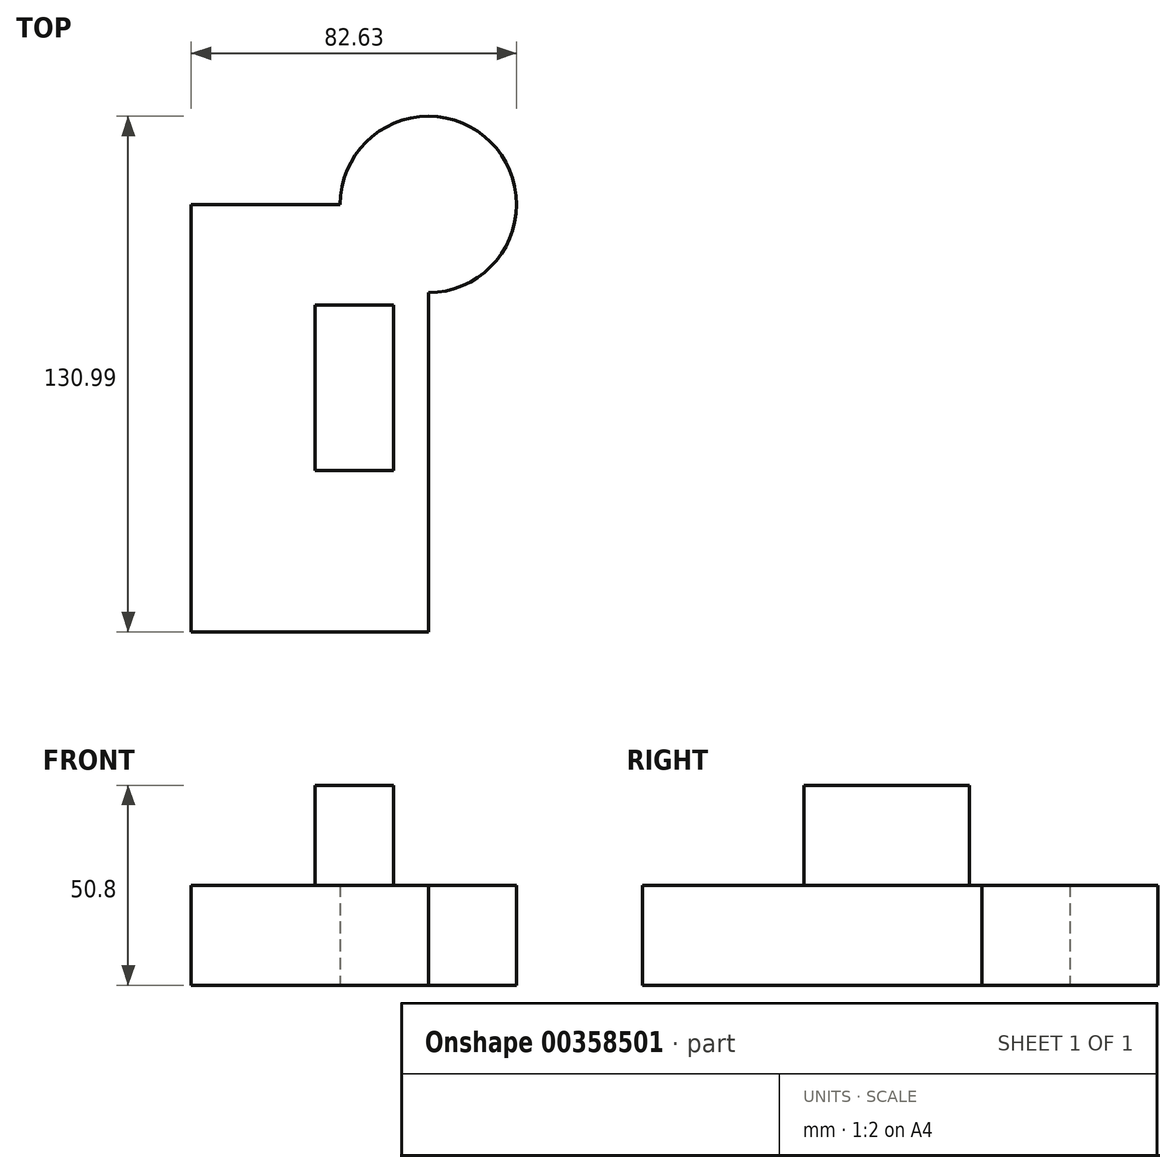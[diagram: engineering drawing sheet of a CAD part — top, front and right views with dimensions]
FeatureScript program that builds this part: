
annotation { "Feature Type Name" : "Feature", "Feature Type Description" : "" }
export const myFeature = defineFeature(function(context is Context, id is Id, definition is map)
    precondition{}
    {
        {
            var Q0;
            Q0=qCreatedBy(makeId("Top.planeOp"),FACE);
            var sketch = newSketch(context, id + "F0", { "sketchPlane" : qUnion([Q0])});
            skLineSegment(sketch, "E0.bottom", {"start": v(2.73, -58.58) * mm, "end": v(62.95, -58.58) * mm});
            skLineSegment(sketch, "E0.top", {"start": v(2.73, 50) * mm, "end": v(62.95, 50) * mm});
            skLineSegment(sketch, "E0.left", {"start": v(2.73, -58.58) * mm, "end": v(2.73, 50) * mm});
            skLineSegment(sketch, "E0.right", {"start": v(62.95, -58.58) * mm, "end": v(62.95, 50) * mm});
            skCircle(sketch, "E1", {"center": v(62.95, 50) * mm, "radius": 22.4 * mm});
            skSolve(sketch);
        }
        {
            var Q0;
            Q0 = qSketchRegion(id + "F0", true);
            extrude(context, id + "F1", {"entities" : qUnion([Q0]), "depth" : 25.4 * mm});
        }
        {
            var Q0;
            Q0=makeQuery(id+"F1.opExtrude","CAP_FACE",FACE,{"disambiguationData":[OSD([sQuery(id+"F0.wireOp",EDGE,"E0.bottom"),sQuery(id+"F0.wireOp",EDGE,"E0.top"),sQuery(id+"F0.wireOp",EDGE,"E0.left"),sQuery(id+"F0.wireOp",EDGE,"E0.right"),sQuery(id+"F0.wireOp",EDGE,"E1")])],"isStart":false});
            var sketch = newSketch(context, id + "F2", { "sketchPlane" : qUnion([Q0])});
            skLineSegment(sketch, "E2.bottom", {"start": v(34.11, -17.61) * mm, "end": v(54.13, -17.61) * mm});
            skLineSegment(sketch, "E2.top", {"start": v(34.11, 24.46) * mm, "end": v(54.13, 24.46) * mm});
            skLineSegment(sketch, "E2.left", {"start": v(34.11, -17.61) * mm, "end": v(34.11, 24.46) * mm});
            skLineSegment(sketch, "E2.right", {"start": v(54.13, -17.61) * mm, "end": v(54.13, 24.46) * mm});
            skSolve(sketch);
        }
        {
            var Q0;
            Q0 = qSketchRegion(id + "F2", true);
            extrude(context, id + "F3", {"entities" : qUnion([Q0]), "operationType" : NewBodyOperationType.ADD, "depth" : 25.4 * mm});
        }
    });
